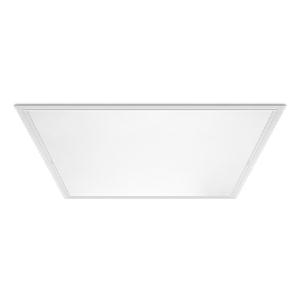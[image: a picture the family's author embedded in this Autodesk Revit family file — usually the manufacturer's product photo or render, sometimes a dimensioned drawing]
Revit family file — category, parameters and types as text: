
# Revit family: 3f_filippi_-_l_340_luce_diffusa_vs_ip65v_3f_filippi_-_23897_-_l_340_25w-840_vs_ip65v_596x596
name_source: partatom
category: Lighting Fixtures
units: mm (PartAtom-declared; Revit-internal decimal feet)

## family parameters
Cut with Voids When Loaded = No
Host = Face
Light Source = No
Part Type = Normal
Room Calculation Point = No
Round Connector Dimension = Use Diameter
Shared = No

## types (1)
- 3F Filippi - L 340 Luce Diffusa VS IP65V (1 x LED, 3499 lm, 29 W, 4000 K)
    Apparent Load = 29 VA
    Approval mark = ENEC
    CIE Flux Codes = 61 89 98 100 100
    Color Rendering = 80
    Color Temperature = 4000 K
    Control Gear = Electronic ballast
    Default Elevation = 1800 mm
    Description = ILLUMINOTECHNICAL
Luminous efficiency 100% (DLOR 100%, ULOR 0%).
Initial luminous flux of the luminaire 3499 lm.
Direct symmetric distribution.
Installation Interdistance Transv.D = 1.17 x hu - Long.D = 1.14 x hu.
Average luminance <3000 cd/m² for radial angles >65°.
Tabular UGR (CIE 117 - 4H-8H; S=0.25H; 70/50/20): RUG 17.6 - 17.4.
Beam angle: 91° - 88°.
Luminous efficacy 121 lm/W.
Lifetime (L93/B10): 30000 h. (tq+25°C)
Lifetime (L90/B10): 50000 h. (tq+25°C)
Lifetime (L85/B10): 80000 h. (tq+25°C)
Lifetime (L80/B10): 100000 h. (tq+25°C)
Sudden decreased luminous flux after 50000 hours: 0% (C0).
Photobiological safety in compliance with IEC/TR 62778: RG0 risk exempt, (IEC 62471).
In compliance with IEC/EN 62722-2-1 - IEC/EN 62717 standards.

SOURCE
Squared LED module 25W/840.
Energy efficiency class (UE 2019/2020 - UE 2019/2015): C.
CIE 13.3 Colour rendering index: CRI >80 (R9 <50%).
IES TM-30 Fidelity Index: Rf = 84 Rg = 95.
CCT nominal colour temperature 4000 K.
Colour initial tolerance (MacAdam): SDCM 3.

MECHANICAL
Housing in hot-galvanised steel, painted in white polyester.
Perimetral frame in white polycarbonate.
VS moulded glass, anti-glare, tempered, non-combustible, thickness 4 mm.
Luminaire with limited surface temperature. - D - (EN 60598-2-24)
Dimensions: 596x596 mm, height 80 mm. Weight 6.4 kg.
IP65 protection degree for exposed part, IP40 for recessed part.
Mechanical strength to impacts IK08 (5 joule).
Glow-wire test resistance 960°C.

ELECTRICAL
Wiring on a separate unit.
Halogen Free electronic wiring 230V-50/60Hz, power factor 0.95, THD <25%, constant output current, SELV, class II, 1 driver.
Power of the luminaire 29 W.
CE - IEC 60598-1 - EN 60598-1.
SAFE FLICKER: PstLM=<1 and SVM=<0.4 (IEC TR 61547-1 and IEC TR 63158), to ensure a more comfortable and safe light.
Luminaire compliant with EN 60598-2-22 for power supply from a centralised emergency system CPSS (Central Power Supply System), not incorporated in the luminaire - high risk areas excluded. The default power and flux are 100% in AC and 100% in DC.
Ambient temperature from 0°C to +40°C.
Temperature class T6 max 85°C.
Relative humidity UR: <85%.

INSTALLATION
Lay-on or pull-up recessed fitting using frame and anti-fall safety cable accessories.
All accessories dedicated to this product are available on the Catalog and on our website www.3F-Filippi.com.

APPLICATIONS
In environments requiring protection and simplified cleaning.
Hospitals, pharmaceutical, chemical, aseptic laboratories, sterilised rooms.
Environments: with VDTs, meeting rooms, offices.
Environments: architectural, commercial, staterooms, banks.
Environments where demanding visual tasks are performed and soft diffuse light is required for optimal visual comfort and total shielding of the light source.

WARNING
Luminaire designed for disposal/recycling at end-of-life.
Replaceable (LED only) light source by a professional. Replaceable control gear by a professional.
    Height = 0 mm  [stored 0 ft]
    Lamp = 1 x LED
    Lamp Light Flux = 3499 lm
    Lamp Power = 29 W
    Lamp count = 1
    Length = 596 mm
    Lifetime = 50000 h
    Luminous efficacy = 121 lm/W
    Manufacturer = 3F Filippi
    ModVariant = No
    Model = 3F Filippi - 23897 - L 340 25W-840 VS IP65V 596x596
    Mounting Place = Ceiling
    Mounting Type = Recessed
    Number of Poles = 1
    OnlyDefault = Yes
    Power Factor = 1
    Product Name = 3F Filippi - L 340 Luce Diffusa VS IP65V
    Product group = recessed luminaire
    ProductGroupID = 4
    Protection Class = Protection class II
    Protection Degree = IP 40
    RLX_Detail_Level = 1
    RLX_Emergency_Light_Flux = 0 lm
    RLX_Emergency_Type = 0
    RLX_Emergency_Type_DB = No
    RlxData = <blob elided: 153221 chars, md5=1a6f22df>
    Socket = socket
    Standby Power = 0 W
    System Light Flux = 3499 lm
    System Power = 29 W
    Type Comments = Product without accessories
    Type Image = 3ffilippi_l_340_luce_diffusa_vs.jpg
    URL = http://relux.com
    VarID = ---
    Voltage = 0 V
    Weight = 0.00 kg
    Width = 596 mm

note: [stored X ft] marks values corroborated as IEEE doubles in the binary element streams (Revit-internal decimal feet)

## geometry (parser evidence)
native form markers: Blend x4, Sweep x12
no freeform markers — native parametric forms only
